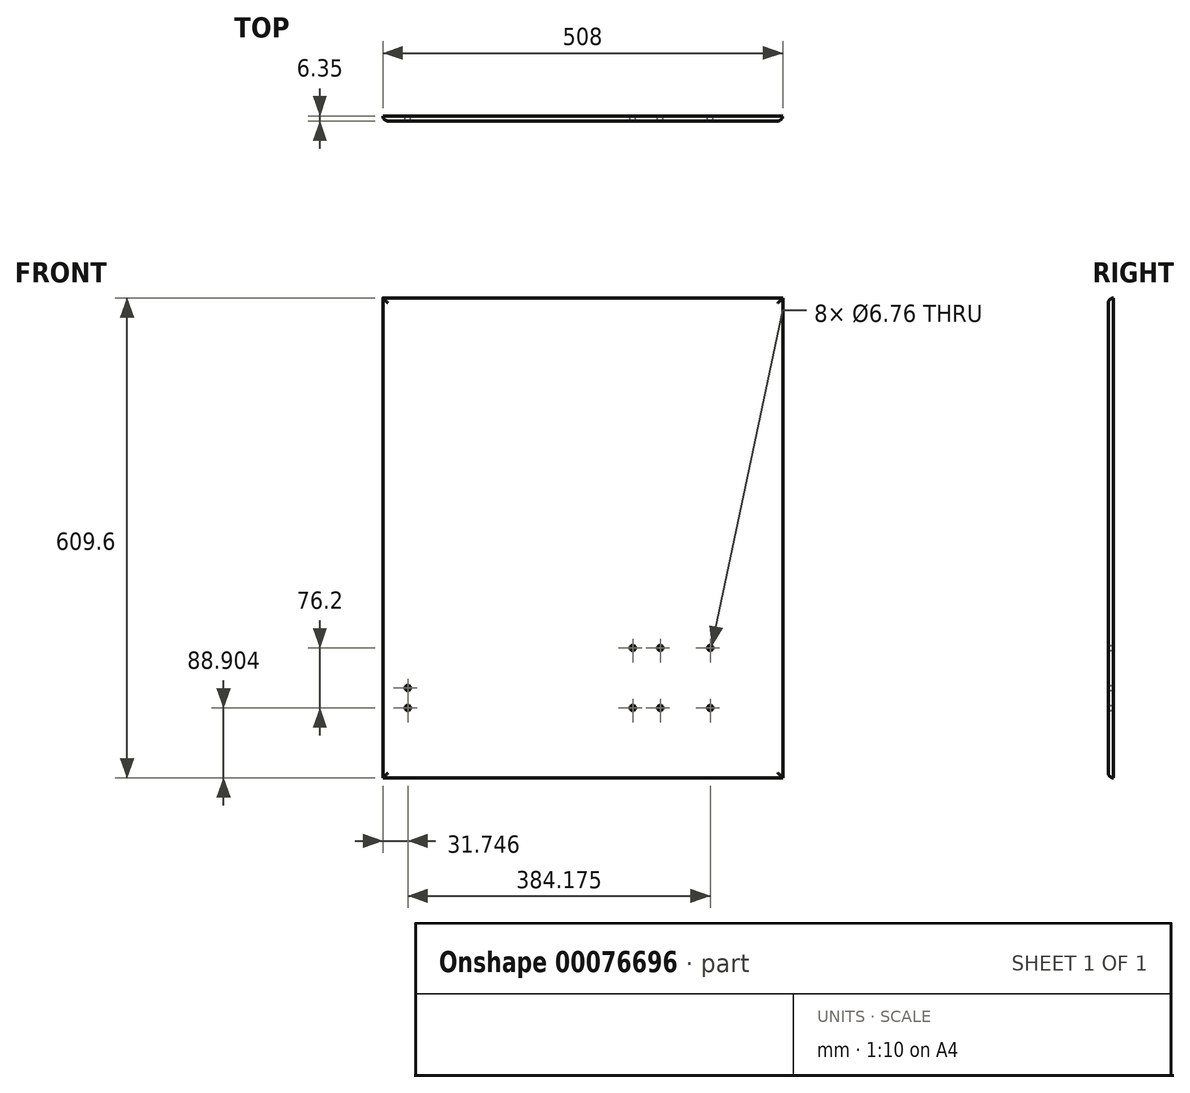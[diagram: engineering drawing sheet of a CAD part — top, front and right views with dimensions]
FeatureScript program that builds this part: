
annotation { "Feature Type Name" : "Feature", "Feature Type Description" : "" }
export const myFeature = defineFeature(function(context is Context, id is Id, definition is map)
    precondition{}
    {
        {
            var Q0;
            Q0=qCreatedBy(makeId("Front.planeOp"),FACE);
            var sketch = newSketch(context, id + "F0", { "sketchPlane" : qUnion([Q0])});
            skLineSegment(sketch, "E0.top", {"start": v(-494.61, -45) * mm, "end": v(13.39, -45) * mm});
            skLineSegment(sketch, "E0.left", {"start": v(-494.61, 259.8) * mm, "end": v(-494.61, -45) * mm});
            skLineSegment(sketch, "E0.right", {"start": v(13.39, 259.8) * mm, "end": v(13.39, -45) * mm});
            skLineSegment(sketch, "E1.0", {"start": v(-462.86, 259.8) * mm, "end": v(-462.86, -45) * mm, "construction": true});
            skLineSegment(sketch, "E2.0", {"start": v(-494.61, 43.9) * mm, "end": v(13.39, 43.9) * mm, "construction": true});
            skLineSegment(sketch, "E3.0", {"start": v(-494.61, 69.3) * mm, "end": v(13.39, 69.3) * mm, "construction": true});
            skLineSegment(sketch, "E4.0", {"start": v(-177.11, 259.8) * mm, "end": v(-177.11, -45) * mm, "construction": true});
            skLineSegment(sketch, "E5.0", {"start": v(-494.61, 120.1) * mm, "end": v(13.39, 120.1) * mm, "construction": true});
            skLineSegment(sketch, "E6.0", {"start": v(-142.19, 259.8) * mm, "end": v(-142.19, -45) * mm, "construction": true});
            skLineSegment(sketch, "E7.0", {"start": v(-78.69, 259.8) * mm, "end": v(-78.69, -45) * mm, "construction": true});
            skCircle(sketch, "E8", {"center": v(-462.86, 69.3) * mm, "radius": 3.17 * mm, "construction": true});
            skCircle(sketch, "E9", {"center": v(-462.86, 43.9) * mm, "radius": 3.17 * mm, "construction": true});
            skCircle(sketch, "E10", {"center": v(-177.11, 43.9) * mm, "radius": 3.17 * mm, "construction": true});
            skCircle(sketch, "E11", {"center": v(-142.19, 43.9) * mm, "radius": 3.17 * mm, "construction": true});
            skCircle(sketch, "E12", {"center": v(-78.69, 43.9) * mm, "radius": 3.17 * mm, "construction": true});
            skCircle(sketch, "E13", {"center": v(-78.69, 120.1) * mm, "radius": 3.17 * mm, "construction": true});
            skCircle(sketch, "E14", {"center": v(-142.19, 120.1) * mm, "radius": 3.17 * mm, "construction": true});
            skCircle(sketch, "E15", {"center": v(-177.11, 120.1) * mm, "radius": 3.17 * mm, "construction": true});
            skLineSegment(sketch, "E16.0", {"start": v(-494.61, 564.6) * mm, "end": v(13.39, 564.6) * mm});
            skLineSegment(sketch, "E17", {"start": v(-494.61, 259.8) * mm, "end": v(-494.61, 564.6) * mm});
            skLineSegment(sketch, "E18", {"start": v(13.39, 259.8) * mm, "end": v(13.39, 564.6) * mm});
            skLineSegment(sketch, "E19", {"start": v(13.39, 259.8) * mm, "end": v(-494.61, 259.8) * mm, "construction": true});
            skSolve(sketch);
        }
        {
            var Q0;
            Q0=makeQuery(id+"F0.imprint","IMPRINT",FACE,{"disambiguationData":[TD([[makeQuery(id+"F0.imprint","IMPRINT",EDGE,{"derivedFrom":sQuery(id+"F0.wireOp",EDGE,"E0.top")}),1.0]])]});
            extrude(context, id + "F1", {"entities" : qUnion([Q0]), "depth" : 6.35 * mm});
        }
        {
            var Q0;
            Q0=makeQuery(id+"F1.opExtrude","CAP_FACE",FACE,{"disambiguationData":[OSD([sQuery(id+"F0.wireOp",EDGE,"E0.top"),sQuery(id+"F0.wireOp",EDGE,"E0.left"),sQuery(id+"F0.wireOp",EDGE,"E0.right"),sQuery(id+"F0.wireOp",EDGE,"E16.0"),sQuery(id+"F0.wireOp",EDGE,"E17"),sQuery(id+"F0.wireOp",EDGE,"E18")])],"isStart":false});
            fillet(context, id + "F2", {"entities" : qUnion([Q0]), "radius" : 6.35 * mm, "tangentPropagation" : true, "allowEdgeOverflow" : false});
        }
        {
            var Q0;
            Q0=sQuery(id+"F0.wireOp",VERTEX,"E15.center");
            var Q1;
            Q1=sQuery(id+"F0.wireOp",VERTEX,"E14.center");
            var Q2;
            Q2=sQuery(id+"F0.wireOp",VERTEX,"E13.center");
            var Q3;
            Q3=sQuery(id+"F0.wireOp",VERTEX,"E12.center");
            var Q4;
            Q4=sQuery(id+"F0.wireOp",VERTEX,"E11.center");
            var Q5;
            Q5=sQuery(id+"F0.wireOp",VERTEX,"E10.center");
            var Q6;
            Q6=sQuery(id+"F0.wireOp",VERTEX,"E8.center");
            var Q7;
            Q7=sQuery(id+"F0.wireOp",VERTEX,"E9.center");
            var Q8;
            Q8=makeQuery(id+"F1.opExtrude","SWEPT_BODY",BODY,{"disambiguationData":[OSD([sQuery(id+"F0.wireOp",EDGE,"E0.top"),sQuery(id+"F0.wireOp",EDGE,"E0.left"),sQuery(id+"F0.wireOp",EDGE,"E0.right"),sQuery(id+"F0.wireOp",EDGE,"E16.0"),sQuery(id+"F0.wireOp",EDGE,"E17"),sQuery(id+"F0.wireOp",EDGE,"E18")])]});
            hole(context, id + "F3", {"style" : HoleStyle.SIMPLE, "endStyle" : HoleEndStyle.THROUGH, "oppositeDirection" : true, "standardTappedOrClearance" : lookupTablePath({ "standard" : "ANSI", "fit" : "Normal (ASME)", "size" : "1/4", "type" : "Clearance" }), "standardBlindInLast" : lookupTablePath({ "fit" : "Free", "standard" : "ANSI", "size" : "1/4", "type" : "Clearance" }), "holeDiameter" : 6.76 * mm, "locations" : qUnion([Q0, Q1, Q2, Q3, Q4, Q5, Q6, Q7]), "scope" : qUnion([Q8]), "isTappedThrough" : true});
        }
    });
